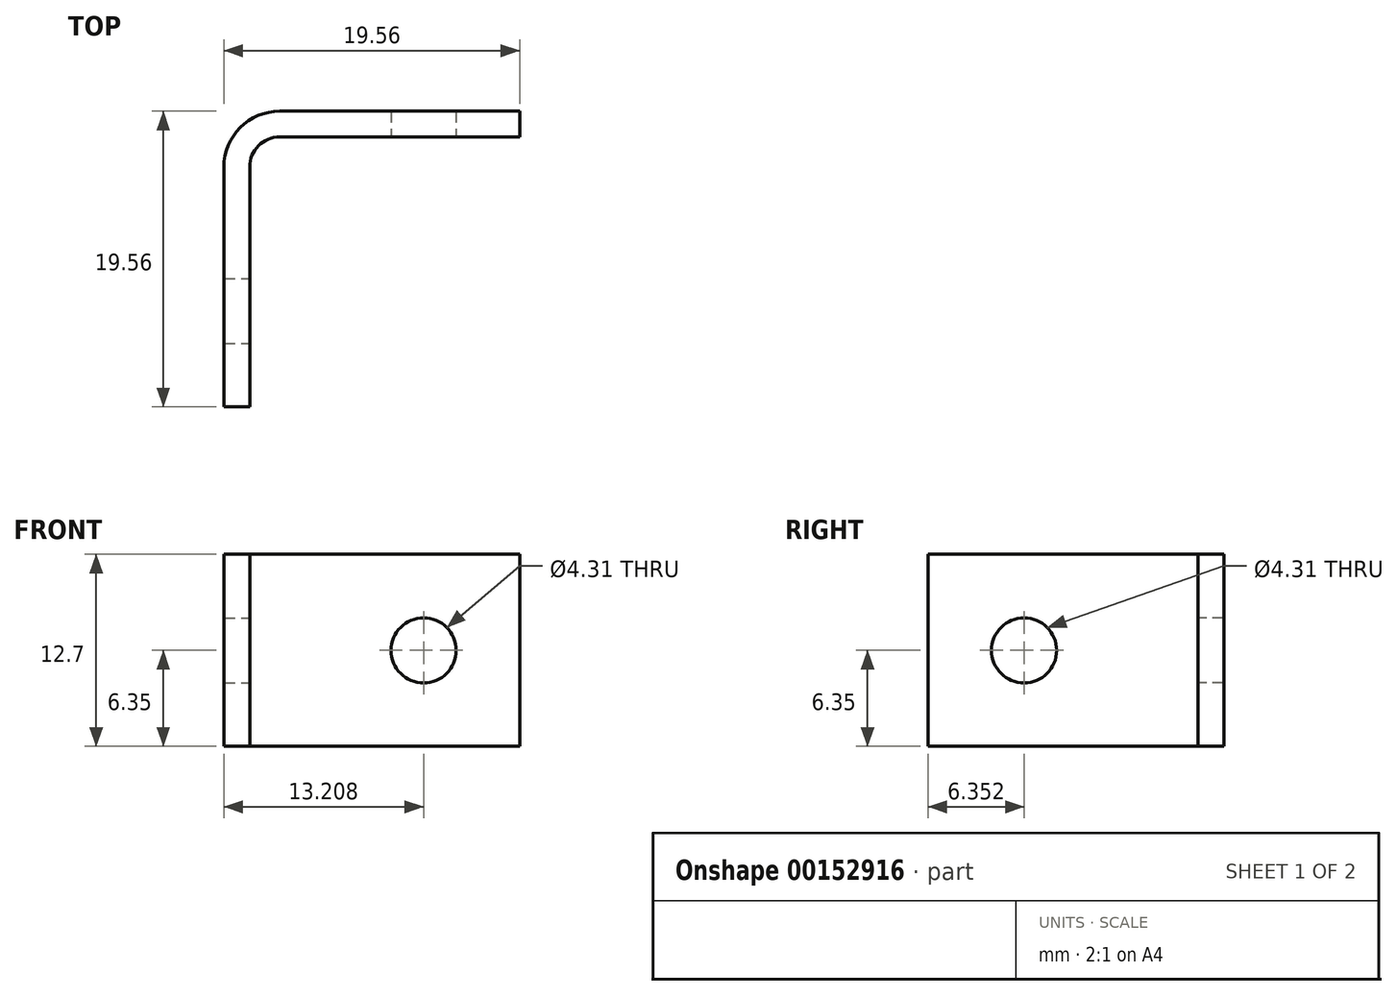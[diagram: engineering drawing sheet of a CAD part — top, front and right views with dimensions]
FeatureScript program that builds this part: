
annotation { "Feature Type Name" : "Feature", "Feature Type Description" : "" }
export const myFeature = defineFeature(function(context is Context, id is Id, definition is map)
    precondition{}
    {
        {
            var Q0;
            Q0=qCreatedBy(makeId("Top.planeOp"),FACE);
            var sketch = newSketch(context, id + "F0", { "sketchPlane" : qUnion([Q0])});
            skLineSegment(sketch, "E0.left", {"start": v(0, 0) * mm, "end": v(0, -19.56) * mm});
            skLineSegment(sketch, "E0.right", {"start": v(1.7, -1.7) * mm, "end": v(1.7, -19.56) * mm});
            skLineSegment(sketch, "E1.top", {"start": v(1.7, -19.56) * mm, "end": v(0, -19.56) * mm});
            skLineSegment(sketch, "E2.bottom", {"start": v(0, 0) * mm, "end": v(19.56, 0) * mm});
            skLineSegment(sketch, "E2.top", {"start": v(1.7, -1.7) * mm, "end": v(19.56, -1.7) * mm});
            skLineSegment(sketch, "E2.right", {"start": v(19.56, -1.7) * mm, "end": v(19.56, 0) * mm});
            skSolve(sketch);
        }
        {
            var Q0;
            Q0=qSketchRegion(id+"F0",true);
            extrude(context, id + "F1", {"entities" : qUnion([Q0]), "depth" : 12.7 * mm});
        }
        {
            var Q0;
            Q0=makeQuery(id+"F1.opExtrude","SWEPT_EDGE",EDGE,{"disambiguationData":[OSD([sQuery(id+"F0.wireOp",EDGE,"E0.right"),sQuery(id+"F0.wireOp",EDGE,"E2.top")])]});
            fillet(context, id + "F2", {"entities" : qUnion([Q0]), "radius" : 1.98 * mm, "tangentPropagation" : true, "allowEdgeOverflow" : false});
        }
        {
            var Q0;
            Q0=makeQuery(id+"F1.opExtrude","SWEPT_EDGE",EDGE,{"disambiguationData":[OSD([sQuery(id+"F0.wireOp",EDGE,"E0.left"),sQuery(id+"F0.wireOp",EDGE,"E2.bottom")])]});
            fillet(context, id + "F3", {"entities" : qUnion([Q0]), "radius" : 3.7 * mm, "tangentPropagation" : true, "allowEdgeOverflow" : false});
        }
        {
            var Q0;
            Q0=makeQuery(id+"F1.opExtrude","SWEPT_FACE",FACE,{"disambiguationData":[OSD([sQuery(id+"F0.wireOp",EDGE,"E2.top")])]});
            var sketch = newSketch(context, id + "F4", { "sketchPlane" : qUnion([Q0])});
            skLineSegment(sketch, "E3.bottom", {"start": v(19.56, 6.35) * mm, "end": v(13.2, 6.35) * mm, "construction": true});
            skLineSegment(sketch, "E3.top", {"start": v(19.56, 12.7) * mm, "end": v(13.2, 12.7) * mm, "construction": true});
            skLineSegment(sketch, "E3.left", {"start": v(19.56, 6.35) * mm, "end": v(19.56, 12.7) * mm, "construction": true});
            skLineSegment(sketch, "E3.right", {"start": v(13.2, 6.35) * mm, "end": v(13.2, 12.7) * mm, "construction": true});
            skCircle(sketch, "E4", {"center": v(13.2, 6.35) * mm, "radius": 2.15 * mm});
            skSolve(sketch);
        }
        {
            var Q0;
            Q0 = qSketchRegion(id + "F4", true);
            var Q1;
            Q1=makeQuery(id+"F1.opExtrude","SWEPT_FACE",FACE,{"disambiguationData":[OSD([sQuery(id+"F0.wireOp",EDGE,"E2.bottom")])]});
            extrude(context, id + "F5", {"entities" : qUnion([Q0]), "operationType" : NewBodyOperationType.REMOVE, "endBound" : BoundingType.UP_TO_SURFACE, "oppositeDirection" : true, "endBoundEntityFace" : qUnion([Q1]), "depth" : 25.4 * mm});
        }
        {
            var Q0;
            Q0=makeQuery(id+"F1.opExtrude","SWEPT_FACE",FACE,{"disambiguationData":[OSD([sQuery(id+"F0.wireOp",EDGE,"E0.right")])]});
            var sketch = newSketch(context, id + "F6", { "sketchPlane" : qUnion([Q0])});
            skLineSegment(sketch, "E5.bottom", {"start": v(-19.56, 6.35) * mm, "end": v(-13.2, 6.35) * mm, "construction": true});
            skLineSegment(sketch, "E5.top", {"start": v(-19.56, 12.7) * mm, "end": v(-13.2, 12.7) * mm, "construction": true});
            skLineSegment(sketch, "E5.left", {"start": v(-19.56, 6.35) * mm, "end": v(-19.56, 12.7) * mm, "construction": true});
            skLineSegment(sketch, "E5.right", {"start": v(-13.2, 6.35) * mm, "end": v(-13.2, 12.7) * mm, "construction": true});
            skCircle(sketch, "E6", {"center": v(-13.2, 6.35) * mm, "radius": 2.15 * mm});
            skSolve(sketch);
        }
        {
            var Q0;
            Q0 = qSketchRegion(id + "F6", true);
            var Q1;
            Q1=makeQuery(id+"F1.opExtrude","SWEPT_FACE",FACE,{"disambiguationData":[OSD([sQuery(id+"F0.wireOp",EDGE,"E0.left")])]});
            extrude(context, id + "F7", {"entities" : qUnion([Q0]), "operationType" : NewBodyOperationType.REMOVE, "endBound" : BoundingType.UP_TO_SURFACE, "oppositeDirection" : true, "endBoundEntityFace" : qUnion([Q1]), "depth" : 25.4 * mm});
        }
    });
